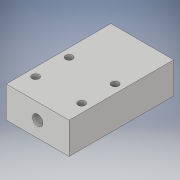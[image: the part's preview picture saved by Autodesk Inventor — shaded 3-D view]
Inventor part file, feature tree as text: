
AUTODESK INVENTOR PART (.ipt)
format: ipt  version: 2018 (Build 220112000, 112)  size: 128,000 bytes
history: native  units: mm
features: sketch x3, extrude x2
ambient origin geometry x8: Origin, YZ Plane, XZ Plane, XY Plane, X Axis, Y Axis, Z Axis, Center Point
bodies: Volumenkörper1 (feature_tree)
feature tree (5):
  sketch  "Skizze1"  dims[d4=15.0mm d5=30.0mm]
  sketch  "Skizze2"  dims[d6=15.0mm d7=7.5mm]
  extrude  "Extrusion1"  Depth=30.0mm
  extrude  "Extrusion2"  Depth=15.0mm
  sketch  "Skizze3"  dims[d8=5.0mm d9=50.0mm d10=0.0mm d11=22.0mm d12=3.4mm d13=3.4mm d14=3.4mm d15=3.4mm d16=4.0mm d17=16.0mm d18=4.0mm d19=16.0mm d20=4.0mm d21=22.0mm d22=10.0mm d23=15.0mm d24=0.0mm]
